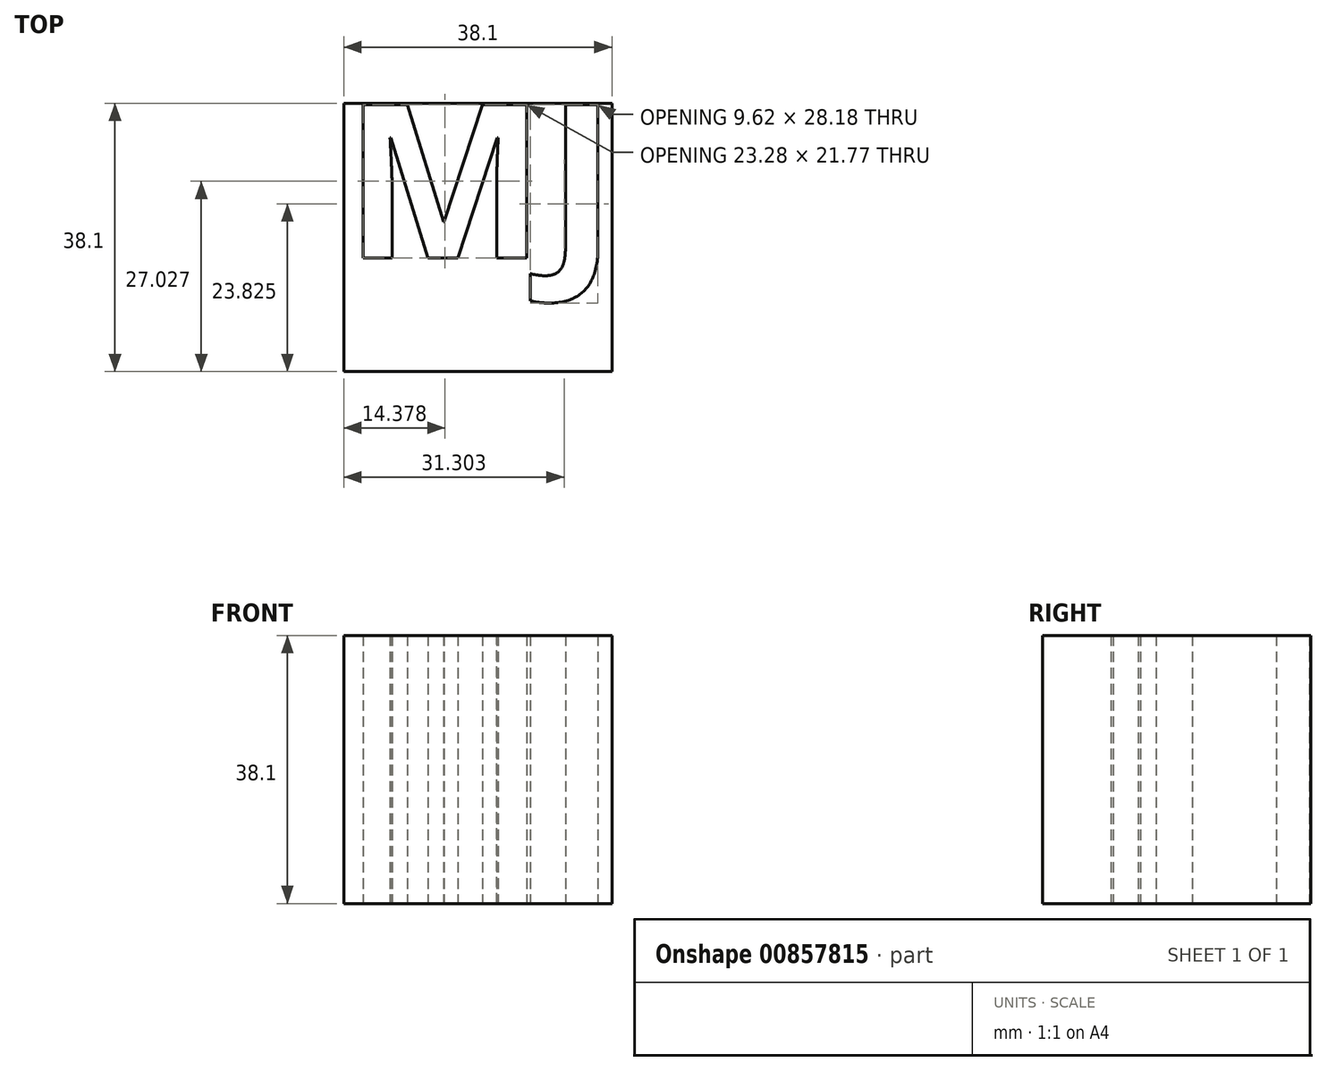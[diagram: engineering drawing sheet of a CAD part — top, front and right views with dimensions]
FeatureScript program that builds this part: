
annotation { "Feature Type Name" : "Feature", "Feature Type Description" : "" }
export const myFeature = defineFeature(function(context is Context, id is Id, definition is map)
    precondition{}
    {
        {
            var Q0;
            Q0=qCreatedBy(makeId("Top.planeOp"),FACE);
            var sketch = newSketch(context, id + "F0", { "sketchPlane" : qUnion([Q0])});
            skLineSegment(sketch, "E0", {"start": v(0, 0) * mm, "end": v(0, 38.1) * mm});
            skLineSegment(sketch, "E1", {"start": v(0, 38.1) * mm, "end": v(38.1, 38.1) * mm});
            skLineSegment(sketch, "E2", {"start": v(38.1, 38.1) * mm, "end": v(38.1, 0) * mm});
            skLineSegment(sketch, "E3", {"start": v(38.1, 0) * mm, "end": v(0, 0) * mm});
            skText(sketch, "E4", { "text": "MJ\n", "fontName": "OpenSans-Bold.ttf"});
            const initialGuessF0  = {"E4": [0, 0.01614, 1, 0, 0.02196]};
            skSetInitialGuess(sketch, initialGuessF0);
            skSolve(sketch);
        }
        {
            var Q0;
            Q0=makeQuery(id+"F0.imprint","IMPRINT",FACE,{"disambiguationData":[TD([[makeQuery(id+"F0.imprint","IMPRINT",EDGE,{"derivedFrom":sQuery(id+"F0.wireOp",EDGE,"E0")}),-1.0]])]});
            extrude(context, id + "F1", {"entities" : qUnion([Q0]), "depth" : 38.1 * mm, "offsetDistance" : 25.4 * mm});
        }
    });
